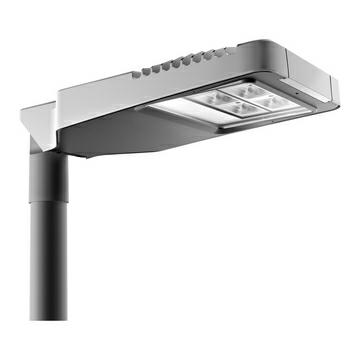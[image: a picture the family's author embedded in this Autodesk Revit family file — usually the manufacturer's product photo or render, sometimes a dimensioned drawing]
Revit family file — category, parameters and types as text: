
# Revit family: Lighting-StreetLighting-GEWISS-ROAD[5]MINI-LED_OPTIC_CYCLE-PEDESTRIAN_CLI
name_source: partatom
category: Apparecchi per illuminazione
units: mm (PartAtom-declared; Revit-internal decimal feet)

## family parameters
Basato su piano di lavoro = No
Condiviso = No
Punto di calcolo locali = No
Quota connettore circolare = Usa diametro
Sempre verticale = Sì
Sorgente d'illuminazione = No
Taglio con vuoti quando caricato = No
Tipo di parte = Normale

## types (4) — shared parameters
Applicazione = External
Catalogue = LIGHTING
Catalogue Range = ROAD [5]
Electrocod = 244C
IDF = 762073c9-db66-42ee-aedc-086dc168bab8
IDT = babf3ceaf7d843279c1ff926cddfbc3c
IP degree = IP66
Immagine tipo = GWR5276M.jpg
Insulation class = I
LED current. = 0,7A
Lamp- = LED
Lampada = LED
Minimum distance from the illuminated object = 1M
Operating temperature: = -25 +50 °C
Power supply operation = Dimmable
Produttore = GEWISS S.p.A.
SEO = Street lighting
Shock resistance = IK08
Technical sheet = https://www.gewiss.com
Tilt adjustable = -20° ÷ +10° side bracket - -10° ÷ +20° pole head
Tipo alimentatore = Constant Current Driver Led
Tipologia = Dimmable
URL = https://www.gewiss.com
Version file RFA = 20.11
Voltage- = 220/240 V - 50/60 Hz - Dimmable 1-10 V
Warranty = 5 years

## per-type parameters (varying)
- GWR5871M30K - ROAD5 MINI CYCL 1M 3000K 0,7A CL1 1-10V: Body=Die-cast aluminium -; Classification:=-; Color Rendering Index=CRI-70; Colore=Graphite grey; Colour :=Powder coating; Colour temperature=3000K; Colour temperature:=3000 K (CRI>80); Context=Street and parking lighting; Control System=Dimmable 1-10 V; DIN 18032-3 certification=-; Descrizione=GWR5871M30K - ROAD5 MINI CYCL 1M 3000K 0,7A CL1 1-10V; Device with reduced surface temperature=-; Driver=Included; Driver Box=Built-in; Efficiency (lm/W)=70; Eletrical and lighting features=-; External screw=Stainless steel; Fixing=Pole Head - Outreach; Gasket=Anti-aging silicone; General information=-; Glow Wire Test :=-; IPEA=ROAD = C // LARGE AREAS = B // CYCLOPEDONALS = C // GREEN AREAS = C // HISTORICAL CENTER = A; Installationa and maintenance=-; LED Life Time (L80B05)=77000H; LED Maintenance=Not available; Lifetime=L90B10 (Tq+25°C) = 100.000 h - L90B10 (Tq+50°C) = 75.000 h; Locking Hook=Integrated front handle; Lumen output (lm)=1900; Luminaire=LED Road Equipment; Materials=-; Maximum surface exposed to the wind=0,149999999999999M2; Maximum surface exposed to the wind :=0.15 m²; Modello=GWR5871M30K; Mouting and installation=Pole Head - Outreach; Nominal flux (lm)=2045; Number of modules=1 (1x3 LED); Operating temperature :=-25 +50 °C; Optic=CYCLE; Optic :=Metallized polycarbonate reflector; Optic Maintenance=Not available; Optic and illuminating features=-; Overvoltage protection=DM 10KV / CM 10KV; Overvoltage resistance :=Common and dfferential mode: 10KV; Photobiological Risk Class=RG0; Rated frequency (Hz)=50 / 60; Shield type=4mm thick flat tempered glass; Standard Deviation Colour Matching=SDCM = 5; Standard-=EN 60598-2-3, EN 60598-1 IEC/TR 62778; Standards and approvals=-; Stocking temperature=-; Supply voltage=220 - 240 V; System power=27W; System power :=27 W @ 0.7A; Tilt-=-20° ÷ +10° side bracket - -10° ÷ +20° pole head; Type of light source=LED - Not replaceable; Unified Glare Rating=G*3 - ULOR = 0; Unique digital code (Datamatrix)=Currently not present; Weight (kg):=6,4; Wiring=Isolating switch
- GWR5872M30K - ROAD5 MINI CYCL 2M 3000K 0,7A CL1 1-10V: Body=Die-cast aluminium -; Classification:=-; Color Rendering Index=CRI-70; Colore=Graphite grey; Colour :=Powder coating; Colour temperature=3000K; Colour temperature:=3000 K (CRI>80); Context=Street and parking lighting; Control System=Dimmable 1-10 V; DIN 18032-3 certification=-; Descrizione=GWR5872M30K - ROAD5 MINI CYCL 2M 3000K 0,7A CL1 1-10V; Device with reduced surface temperature=-; Driver=Included; Driver Box=Built-in; Efficiency (lm/W)=72; Eletrical and lighting features=-; External screw=Stainless steel; Fixing=Pole Head - Outreach; Gasket=Anti-aging silicone; General information=-; Glow Wire Test :=-; IPEA=ROAD = C // LARGE AREAS = B // CYCLOPEDONALS = C // GREEN AREAS = C // HISTORICAL CENTER = A; Installationa and maintenance=-; LED Life Time (L80B05)=77000H; LED Maintenance=Not available; Lifetime=L90B10 (Tq+25°C) = 100.000 h - L90B10 (Tq+50°C) = 75.000 h; Locking Hook=Integrated front handle; Lumen output (lm)=3800; Luminaire=LED Road Equipment; Materials=-; Maximum surface exposed to the wind=0,149999999999999M2; Maximum surface exposed to the wind :=0.15 m²; Modello=GWR5872M30K; Mouting and installation=Pole Head - Outreach; Nominal flux (lm)=4090; Number of modules=2 (2x3 LED); Operating temperature :=-25 +50 °C; Optic=CYCLE; Optic :=Metallized polycarbonate reflector; Optic Maintenance=Not available; Optic and illuminating features=-; Overvoltage protection=DM 10KV / CM 10KV; Overvoltage resistance :=Common and dfferential mode: 10KV; Photobiological Risk Class=RG0; Rated frequency (Hz)=50 / 60; Shield type=4mm thick flat tempered glass; Standard Deviation Colour Matching=SDCM = 5; Standard-=EN 60598-2-3, EN 60598-1 IEC/TR 62778; Standards and approvals=-; Stocking temperature=-; Supply voltage=220 - 240 V; System power=53W; System power :=53 W @ 0.7A; Tilt-=-20° ÷ +10° side bracket - -10° ÷ +20° pole head; Type of light source=LED - Not replaceable; Unified Glare Rating=G*3 - ULOR = 0; Unique digital code (Datamatrix)=Currently not present; Weight (kg):=6,59999999999999; Wiring=Isolating switch
- GWR5871M - ROAD5 MINI CYCL 1M 4000K 0,7A CL1 1-10V: Colour temperature=4000 K (CRI 70); Colour temperature:=4000 K (CRI 70); Descrizione=ROAD5 MINI CYCL 1M 4000K 0,7A CL1 1-10V; EAN code=8011564885332; LED LifeTime (L80B05)=77000H; Lumen output (lm)=1900; Maximum surface exposed to the wind=0,15M2; Modello=GWR5871M; No. Chorus modules=1 (1x3 LED); Nominal flux (lm)=2350; Number of modules=1 (1x3 LED); Optic=Cycle and pedestrian - ULOR: 0%; Overvoltage resistance=12 KV (Common and dfferential mode); Pilot current=0,7A; System power=27W; Weight (kg)=6,4; Weight (kg):=6,4; Working temperature=-25 +50 °C
- GWR5872M - ROAD5 MINI CYCL 2M 4000K 0,7A CL1 1-10V: Colour temperature=4000 K (CRI 70); Colour temperature:=4000 K (CRI 70); Descrizione=ROAD5 MINI CYCL 2M 4000K 0,7A CL1 1-10V; EAN code=8011564885349; LED LifeTime (L80B05)=77000H; Lumen output (lm)=3800; Maximum surface exposed to the wind=0,15M2; Modello=GWR5872M; No. Chorus modules=2 (2x3 LED); Nominal flux (lm)=4700; Number of modules=2 (2x3 LED); Optic=Cycle and pedestrian - ULOR: 0%; Overvoltage resistance=12 KV (Common and dfferential mode); Pilot current=0,7A; System power=53W; Weight (kg)=6,6; Weight (kg):=6,6; Working temperature=-25 +50 °C

## geometry (parser evidence)
native form markers: Blend x2
no freeform markers — native parametric forms only
